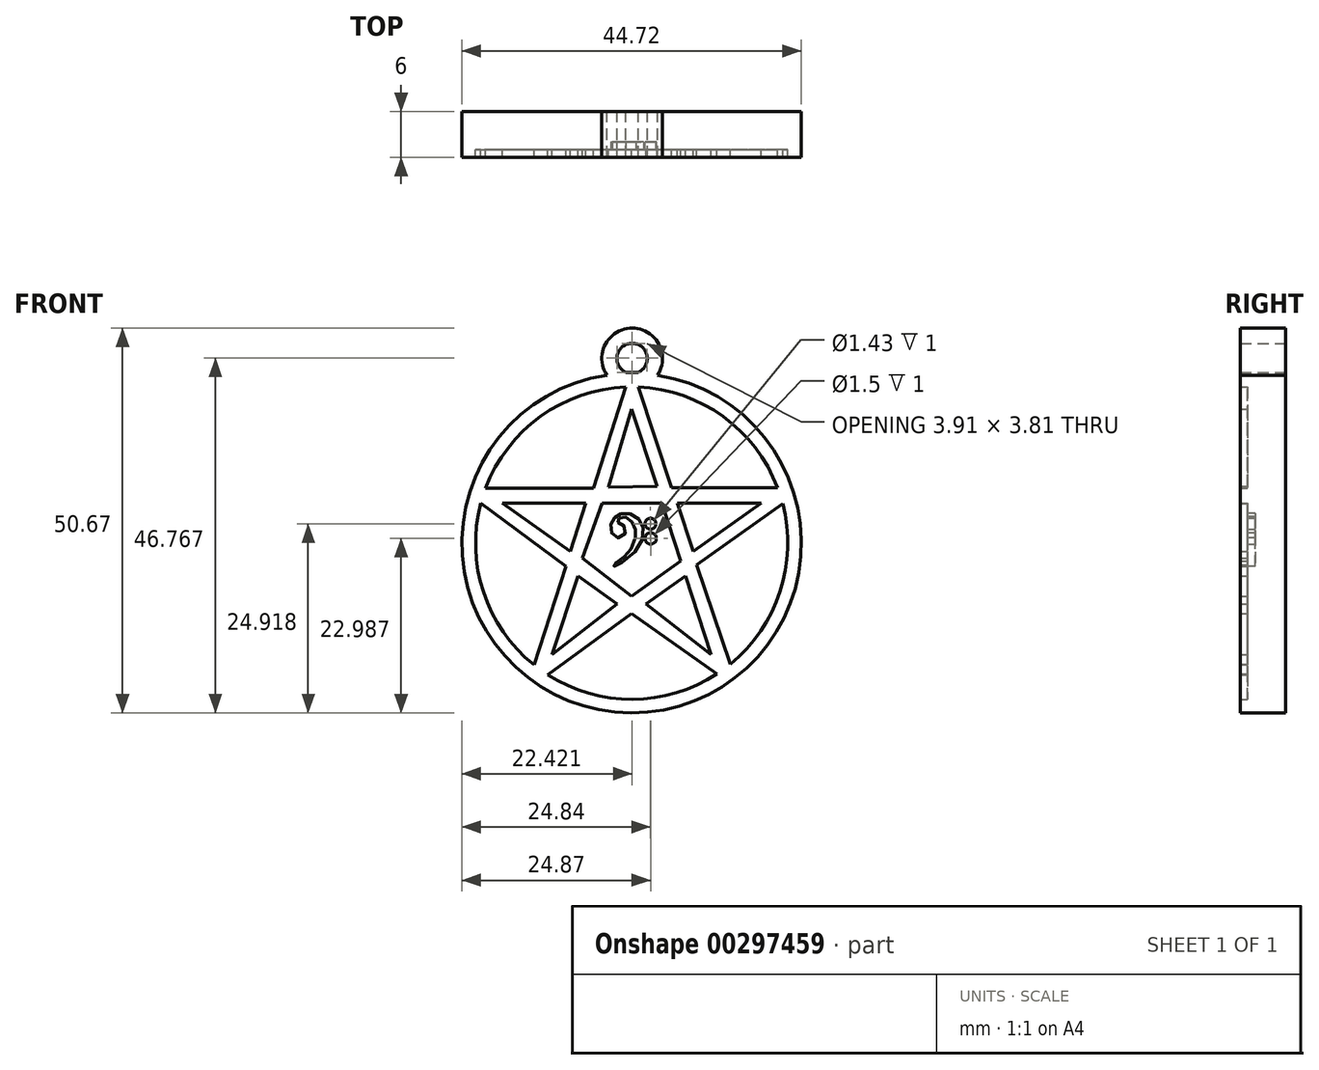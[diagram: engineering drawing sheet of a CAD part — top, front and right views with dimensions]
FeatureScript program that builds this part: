
annotation { "Feature Type Name" : "Feature", "Feature Type Description" : "" }
export const myFeature = defineFeature(function(context is Context, id is Id, definition is map)
    precondition{}
    {
        {
            var Q0;
            Q0=qCreatedBy(makeId("Front.planeOp"),FACE);
            var sketch = newSketch(context, id + "F0", { "sketchPlane" : qUnion([Q0])});
            skLineSegment(sketch, "E0", {"start": v(-45, 0) * mm, "end": v(-22.5, 0) * mm, "construction": true});
            skLineSegment(sketch, "E1", {"start": v(-22.5, 0) * mm, "end": v(-22.5, 45) * mm, "construction": true});
            skLineSegment(sketch, "E2", {"start": v(-22.5, 22.5) * mm, "end": v(0, 22.5) * mm, "construction": true});
            skArc(sketch, "E3", {"start": v(-23.28, 43.05) * mm, "mid": v(-34.53, 39.18) * mm, "end": v(-41.75, 29.73) * mm});
            skArc(sketch, "E4", {"start": v(-25.78, 44.62) * mm, "mid": v(-22.56, 0.14) * mm, "end": v(-19.1, 44.6) * mm});
            skLineSegment(sketch, "E5", {"start": v(-23.28, 43.05) * mm, "end": v(-27.56, 29.73) * mm});
            skLineSegment(sketch, "E6", {"start": v(-27.56, 29.73) * mm, "end": v(-41.75, 29.73) * mm});
            skLineSegment(sketch, "E7", {"start": v(-42.38, 27.74) * mm, "end": v(-31.16, 19.43) * mm});
            skLineSegment(sketch, "E8", {"start": v(-31.16, 19.43) * mm, "end": v(-35.37, 6.47) * mm});
            skLineSegment(sketch, "E9", {"start": v(-33.54, 5.15) * mm, "end": v(-22.5, 13.21) * mm});
            skLineSegment(sketch, "E10", {"start": v(-22.5, 13.21) * mm, "end": v(-11.26, 5.28) * mm});
            skLineSegment(sketch, "E11", {"start": v(-9.5, 6.57) * mm, "end": v(-13.95, 19.66) * mm});
            skLineSegment(sketch, "E12", {"start": v(-13.95, 19.66) * mm, "end": v(-2.6, 27.69) * mm});
            skLineSegment(sketch, "E13", {"start": v(-3.28, 29.81) * mm, "end": v(-17.26, 29.81) * mm});
            skLineSegment(sketch, "E14", {"start": v(-17.26, 29.81) * mm, "end": v(-21.6, 43.04) * mm});
            skLineSegment(sketch, "E15", {"start": v(-25.54, 29.87) * mm, "end": v(-22.5, 40.13) * mm});
            skLineSegment(sketch, "E16", {"start": v(-22.5, 40.13) * mm, "end": v(-19.18, 29.98) * mm});
            skLineSegment(sketch, "E17", {"start": v(-19.18, 29.98) * mm, "end": v(-25.54, 29.87) * mm});
            skLineSegment(sketch, "E18", {"start": v(-16.47, 27.74) * mm, "end": v(-14.4, 21.42) * mm});
            skLineSegment(sketch, "E19", {"start": v(-14.4, 21.42) * mm, "end": v(-5.46, 27.74) * mm});
            skLineSegment(sketch, "E20", {"start": v(-5.46, 27.74) * mm, "end": v(-16.47, 27.74) * mm});
            skLineSegment(sketch, "E21", {"start": v(-20.6, 14.5) * mm, "end": v(-15.41, 18.16) * mm});
            skLineSegment(sketch, "E22", {"start": v(-15.41, 18.16) * mm, "end": v(-12.03, 7.84) * mm});
            skLineSegment(sketch, "E23", {"start": v(-12.03, 7.84) * mm, "end": v(-20.6, 14.5) * mm});
            skLineSegment(sketch, "E24", {"start": v(-22.5, 15.54) * mm, "end": v(-16.01, 20.13) * mm});
            skLineSegment(sketch, "E25", {"start": v(-16.01, 20.13) * mm, "end": v(-18.5, 27.74) * mm});
            skLineSegment(sketch, "E26", {"start": v(-18.5, 27.74) * mm, "end": v(-26.41, 27.74) * mm});
            skLineSegment(sketch, "E27", {"start": v(-26.41, 27.74) * mm, "end": v(-28.97, 20.5) * mm});
            skLineSegment(sketch, "E28.MirrorCS", {"start": v(-28.53, 27.74) * mm, "end": v(-30.6, 21.42) * mm});
            skLineSegment(sketch, "E29.MirrorCS", {"start": v(-39.54, 27.74) * mm, "end": v(-28.53, 27.74) * mm});
            skLineSegment(sketch, "E30.MirrorCS", {"start": v(-30.6, 21.42) * mm, "end": v(-39.54, 27.74) * mm});
            skLineSegment(sketch, "E31.MirrorCS", {"start": v(-24.4, 14.5) * mm, "end": v(-29.59, 18.16) * mm});
            skLineSegment(sketch, "E32.MirrorCS", {"start": v(-32.97, 7.84) * mm, "end": v(-24.4, 14.5) * mm});
            skLineSegment(sketch, "E33.MirrorCS", {"start": v(-29.59, 18.16) * mm, "end": v(-32.97, 7.84) * mm});
            skArc(sketch, "E34.trimOffspring", {"start": v(-3.28, 29.81) * mm, "mid": v(-10.46, 39.17) * mm, "end": v(-21.6, 43.04) * mm});
            skArc(sketch, "E35.trimOffspring", {"start": v(-42.38, 27.74) * mm, "mid": v(-42.03, 16.06) * mm, "end": v(-35.37, 6.47) * mm});
            skArc(sketch, "E36.trimOffspring", {"start": v(-33.54, 5.15) * mm, "mid": v(-22.38, 1.94) * mm, "end": v(-11.26, 5.28) * mm});
            skArc(sketch, "E37.trimOffspring", {"start": v(-9.5, 6.57) * mm, "mid": v(-2.95, 16.12) * mm, "end": v(-2.6, 27.69) * mm});
            skArc(sketch, "E38", {"start": v(-21.6, 45) * mm, "mid": v(-22.44, 48.81) * mm, "end": v(-23.28, 45) * mm});
            skArc(sketch, "E39", {"start": v(-19.1, 44.6) * mm, "mid": v(-22.43, 50.81) * mm, "end": v(-25.78, 44.62) * mm});
            skLineSegment(sketch, "E40", {"start": v(-21.6, 45) * mm, "end": v(-23.28, 45) * mm});
            skLineSegment(sketch, "E41", {"start": v(-28.97, 20.5) * mm, "end": v(-22.5, 15.54) * mm});
            skPoint(sketch, "E42.secondSnap0", {"position": v(-19.26, 17.83) * mm});
            skFitSpline(sketch, "E43", {"points": [v(-24.14, 25.8) * mm, v(-23.82, 25.92) * mm, v(-23.5, 25.98) * mm, v(-22.94, 25.77) * mm, v(-22.65, 25.52) * mm, v(-22.28, 24.98) * mm, v(-22.05, 24.52) * mm, v(-21.94, 23.91) * mm, v(-21.96, 23.54) * mm, v(-22.1, 22.9) * mm, v(-22.67, 21.62) * mm, v(-23.23, 20.92) * mm, v(-23.77, 20.47) * mm, v(-24.42, 20) * mm, v(-25.04, 19.6) * mm, v(-24.98, 19.43) * mm, v(-24.5, 19.64) * mm, v(-24.2, 19.72) * mm, v(-22.68, 20.77) * mm, v(-21.48, 22.16) * mm, v(-20.95, 23.57) * mm, v(-21, 24.6) * mm, v(-21.24, 25.3) * mm, v(-21.94, 26.04) * mm, v(-22.72, 26.4) * mm, v(-23.36, 26.43) * mm, v(-23.97, 26.32) * mm, v(-24.43, 26.11) * mm, v(-24.78, 25.83) * mm, v(-25.09, 25.4) * mm, v(-25.26, 24.96) * mm, v(-25.23, 24.35) * mm, v(-25.12, 23.79) * mm, v(-24.73, 23.33) * mm, v(-24.24, 23.18) * mm, v(-23.63, 23.4) * mm, v(-23.28, 23.96) * mm, v(-23.36, 24.53) * mm, v(-23.62, 24.89) * mm, v(-23.99, 25.08) * mm, v(-24.27, 25.22) * mm, v(-24.4, 25.37) * mm, v(-24.44, 25.56) * mm, v(-24.14, 25.8) * mm]});
            skCircle(sketch, "E44", {"center": v(-20.02, 25.06) * mm, "radius": 0.72 * mm});
            skCircle(sketch, "E45", {"center": v(-19.99, 23.13) * mm, "radius": 0.75 * mm});
            skSolve(sketch);
        }
        {
            var Q0;
            Q0=makeQuery(id+"F0.imprint","IMPRINT",FACE,{"disambiguationData":[TD([[makeQuery(id+"F0.imprint","IMPRINT",EDGE,{"derivedFrom":sQuery(id+"F0.wireOp",EDGE,"E3")}),1.0]])]});
            var Q1;
            Q1=makeQuery(id+"F0.imprint","IMPRINT",FACE,{"disambiguationData":[TD([[makeQuery(id+"F0.imprint","IMPRINT",EDGE,{"derivedFrom":sQuery(id+"F0.wireOp",EDGE,"E7")}),-1.0]])]});
            var Q2;
            Q2=makeQuery(id+"F0.imprint","IMPRINT",FACE,{"disambiguationData":[TD([[makeQuery(id+"F0.imprint","IMPRINT",EDGE,{"derivedFrom":sQuery(id+"F0.wireOp",EDGE,"E9")}),-1.0]])]});
            var Q3;
            Q3=makeQuery(id+"F0.imprint","IMPRINT",FACE,{"disambiguationData":[TD([[makeQuery(id+"F0.imprint","IMPRINT",EDGE,{"derivedFrom":sQuery(id+"F0.wireOp",EDGE,"E11")}),-1.0]])]});
            var Q4;
            Q4=makeQuery(id+"F0.imprint","IMPRINT",FACE,{"disambiguationData":[TD([[makeQuery(id+"F0.imprint","IMPRINT",EDGE,{"derivedFrom":sQuery(id+"F0.wireOp",EDGE,"E13")}),-1.0]])]});
            var Q5;
            Q5=makeQuery(id+"F0.imprint","IMPRINT",FACE,{"disambiguationData":[TD([[makeQuery(id+"F0.imprint","IMPRINT",EDGE,{"derivedFrom":sQuery(id+"F0.wireOp",EDGE,"E3")}),-1.0]])]});
            var Q6;
            Q6=makeQuery(id+"F0.imprint","IMPRINT",FACE,{"disambiguationData":[TD([[makeQuery(id+"F0.imprint","IMPRINT",EDGE,{"derivedFrom":sQuery(id+"F0.wireOp",EDGE,"E18")}),1.0]])]});
            var Q7;
            Q7=makeQuery(id+"F0.imprint","IMPRINT",FACE,{"disambiguationData":[TD([[makeQuery(id+"F0.imprint","IMPRINT",EDGE,{"derivedFrom":sQuery(id+"F0.wireOp",EDGE,"E28.MirrorCS")}),-1.0]])]});
            var Q8;
            Q8=makeQuery(id+"F0.imprint","IMPRINT",FACE,{"disambiguationData":[TD([[makeQuery(id+"F0.imprint","IMPRINT",EDGE,{"derivedFrom":sQuery(id+"F0.wireOp",EDGE,"E15")}),-1.0]])]});
            var Q9;
            Q9=makeQuery(id+"F0.imprint","IMPRINT",FACE,{"disambiguationData":[TD([[makeQuery(id+"F0.imprint","IMPRINT",EDGE,{"derivedFrom":sQuery(id+"F0.wireOp",EDGE,"E31.MirrorCS")}),1.0]])]});
            var Q10;
            Q10=makeQuery(id+"F0.imprint","IMPRINT",FACE,{"disambiguationData":[TD([[makeQuery(id+"F0.imprint","IMPRINT",EDGE,{"derivedFrom":sQuery(id+"F0.wireOp",EDGE,"E21")}),-1.0]])]});
            var Q11;
            Q11=makeQuery(id+"F0.imprint","IMPRINT",FACE,{"disambiguationData":[TD([[makeQuery(id+"F0.imprint","IMPRINT",EDGE,{"derivedFrom":sQuery(id+"F0.wireOp",EDGE,"E24")}),1.0]])]});
            extrude(context, id + "F1", {"entities" : qUnion([Q0, Q1, Q2, Q3, Q4, Q5, Q6, Q7, Q8, Q9, Q10, Q11]), "depth" : 5 * mm});
        }
        {
            var Q0;
            Q0=makeQuery(id+"F0.imprint","IMPRINT",FACE,{"disambiguationData":[TD([[makeQuery(id+"F0.imprint","IMPRINT",EDGE,{"derivedFrom":sQuery(id+"F0.wireOp",EDGE,"E3")}),-1.0]])]});
            extrude(context, id + "F2", {"entities" : qUnion([Q0]), "operationType" : NewBodyOperationType.ADD, "depth" : 6 * mm});
        }
        {
            var Q0;
            Q0=makeQuery(id+"F0.imprint","IMPRINT",FACE,{"disambiguationData":[TD([[makeQuery(id+"F0.imprint","IMPRINT",EDGE,{"derivedFrom":sQuery(id+"F0.wireOp",EDGE,"E43")}),1.0]])]});
            var Q1;
            Q1=makeQuery(id+"F0.imprint","IMPRINT",FACE,{"disambiguationData":[TD([[makeQuery(id+"F0.imprint","IMPRINT",EDGE,{"derivedFrom":sQuery(id+"F0.wireOp",EDGE,"E44")}),1.0]])]});
            var Q2;
            Q2=makeQuery(id+"F0.imprint","IMPRINT",FACE,{"disambiguationData":[TD([[makeQuery(id+"F0.imprint","IMPRINT",EDGE,{"derivedFrom":sQuery(id+"F0.wireOp",EDGE,"E45")}),1.0]])]});
            extrude(context, id + "F3", {"entities" : qUnion([Q0, Q1, Q2]), "operationType" : NewBodyOperationType.ADD, "depth" : 4 * mm});
        }
    });
